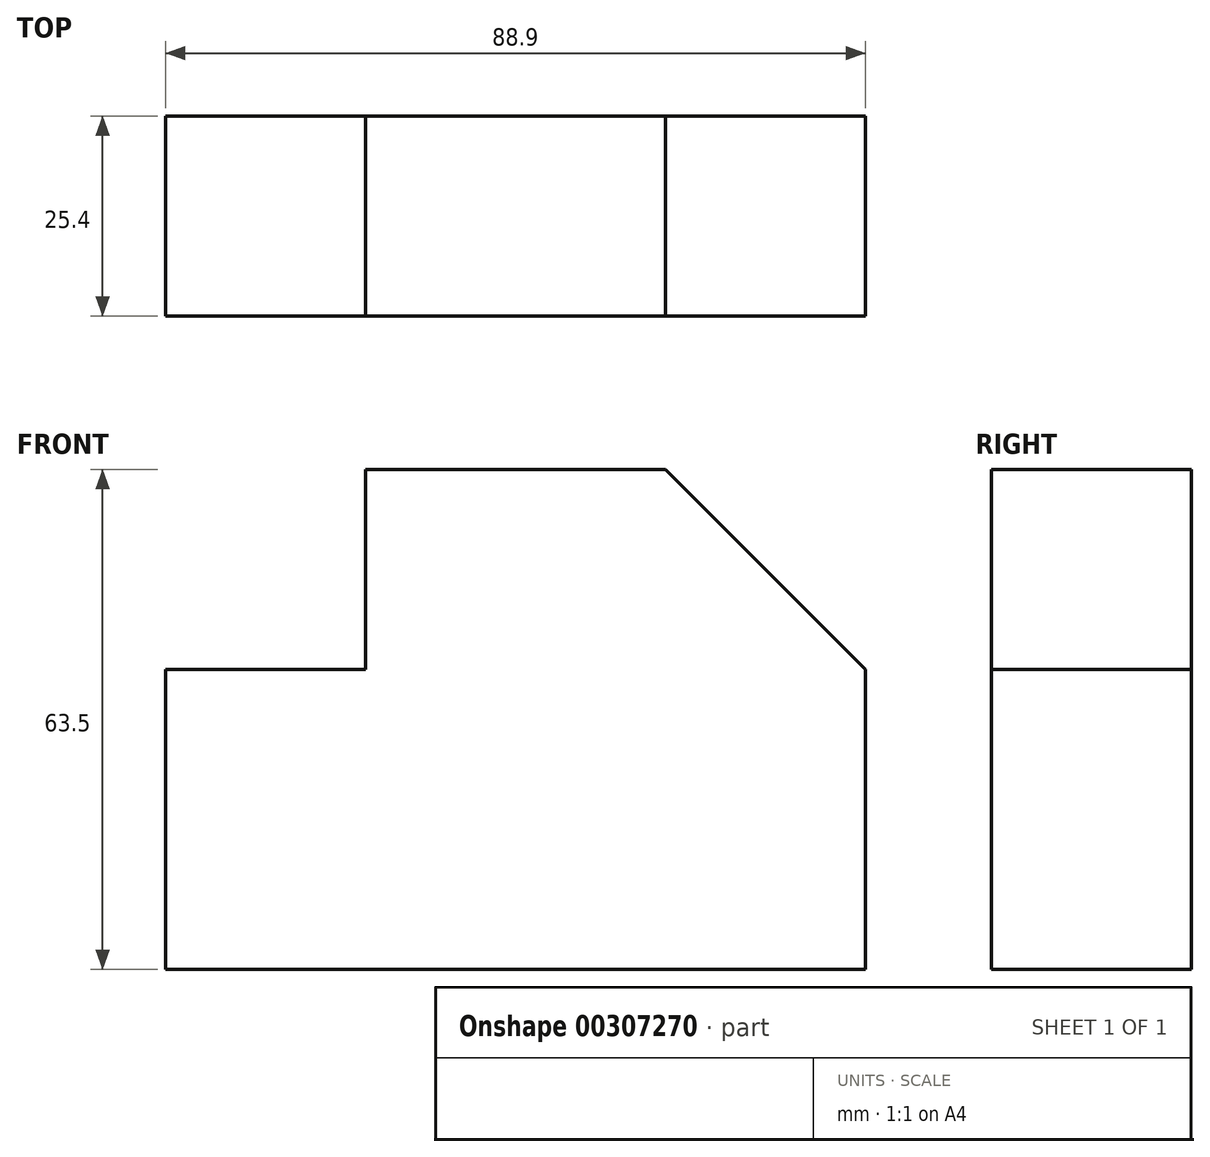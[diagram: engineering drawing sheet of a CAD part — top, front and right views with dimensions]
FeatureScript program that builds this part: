
annotation { "Feature Type Name" : "Feature", "Feature Type Description" : "" }
export const myFeature = defineFeature(function(context is Context, id is Id, definition is map)
    precondition{}
    {
        {
            var Q0;
            Q0=qCreatedBy(makeId("Front.planeOp"),FACE);
            var sketch = newSketch(context, id + "F0", { "sketchPlane" : qUnion([Q0])});
            skLineSegment(sketch, "E0", {"start": v(-52.19, -70.17) * mm, "end": v(36.71, -70.17) * mm});
            skLineSegment(sketch, "E1", {"start": v(36.71, -70.17) * mm, "end": v(36.71, -32.07) * mm});
            skLineSegment(sketch, "E2", {"start": v(-52.19, -70.17) * mm, "end": v(-52.19, -32.07) * mm});
            skLineSegment(sketch, "E3", {"start": v(-52.19, -32.07) * mm, "end": v(-26.79, -32.07) * mm});
            skLineSegment(sketch, "E4", {"start": v(-26.79, -32.07) * mm, "end": v(-26.79, -6.67) * mm});
            skLineSegment(sketch, "E5", {"start": v(-26.79, -6.67) * mm, "end": v(11.31, -6.67) * mm});
            skLineSegment(sketch, "E6", {"start": v(11.31, -6.67) * mm, "end": v(36.71, -32.07) * mm});
            skSolve(sketch);
        }
        {
            var Q0;
            Q0=makeQuery(id+"F0.imprint","IMPRINT",FACE,{"disambiguationData":[TD([[makeQuery(id+"F0.imprint","IMPRINT",EDGE,{"derivedFrom":sQuery(id+"F0.wireOp",EDGE,"E0")}),1.0]])]});
            extrude(context, id + "F1", {"entities" : qUnion([Q0]), "depth" : 25.4 * mm});
        }
    });
